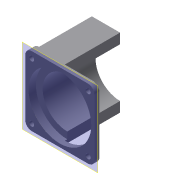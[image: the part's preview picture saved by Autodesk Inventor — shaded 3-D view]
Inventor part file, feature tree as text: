
AUTODESK INVENTOR PART (.ipt)
format: ipt  version: 2022 (Build 260153000, 153)  size: 188,928 bytes
history: native  units: mm
features: extrude x5, sketch x5, plane x2, projected_geometry x2, other x2, reference x1
ambient origin geometry x8: Origin, YZ Plane, XZ Plane, XY Plane, X Axis, Y Axis, Z Axis, Center Point
bodies: Body1 (feature_tree)
feature tree (17):
  plane  "Work Plane3"
  extrude  "Extrusion2"  Depth=25.5mm
  sketch  "Sketch3"  dims[d5=0.0mm d6=0.0mm]
  plane  "Work Plane4"
  extrude  "Extrusion3"  TaperAngle=0.0deg  [1 undecoded]
  extrude  "Extrusion4"  TaperAngle=0.0deg  [1 undecoded]
  extrude  "Extrusion5"  Depth=3.0mm
  extrude  "Extrusion6"  Depth=15.0mm TaperAngle=0.0deg
  sketch  "Sketch2"  dims[d3=0.1mm d4=25.5mm]
  reference  "Reference6"
  projected_geometry  "Projected Loop1"
  sketch  "Sketch4"  dims[d7=0.0mm d8=0.0mm]
  sketch  "Sketch5"  dims[d9=3.0mm d10=0.0mm d11=20.0mm]
  sketch  "Sketch6"  dims[d12=21.5mm d13=0.0mm d14=15.0mm d15=0.0mm d16=2.8mm d17=2.8mm d18=15.0mm d19=0.0mm d20=1.0mm d21=0.0mm]
  projected_geometry  "Projected Loop2"
  other  "Assembly_Cube_Z_Focus_MGN_NEMA_v3.iam"
  other  "00_NEMA11:1"
note: 2 required parameter values undecoded (feature->parameter linkage not recoverable at this tier; creation-order binding heuristic only, values carry confidence <= 0.55)
